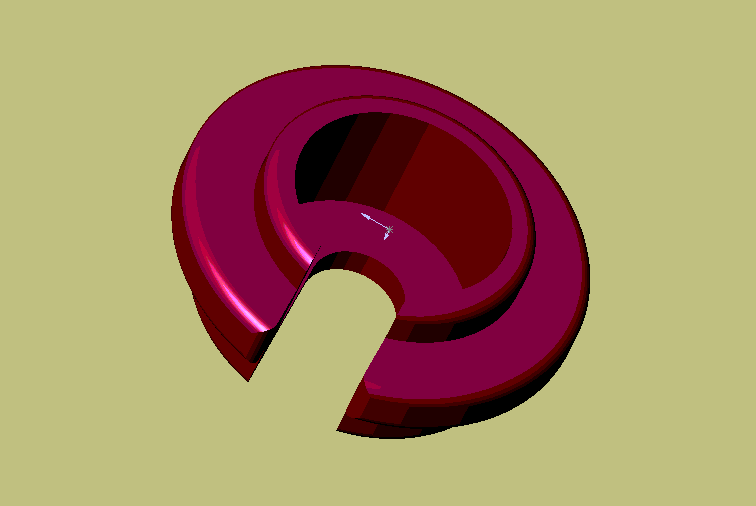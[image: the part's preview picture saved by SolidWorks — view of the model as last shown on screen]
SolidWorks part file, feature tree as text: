
SOLIDWORKS PART (.sldprt)
format: sldprt  version: not decoded by parser v0  size: 251,392 bytes
history: native  units: mm
features: sketch x5, plane x3, extrude x3, cut_extrude x2, material x1, fillet x1 (+8 scaffold rows collapsed)
feature tree (23):
  scaffold x8  (default folders/planes/origin — collapsed)
  material  "Matériau <non spécifié>"
  plane  "Plane1"
  plane  "Plane2"
  plane  "Plane3"
  sketch  "Esquisse1"  dims[D1=15.0mm]
  extrude  "Base-Extrusion"  Depth=2mm
  sketch  "Esquisse2"  dims[D1=12.0mm]
  extrude  "Boss.-Extru.1"  Depth=2.5mm
  sketch  "Esquisse3"  dims[D1=10.0mm]
  extrude  "Boss.-Extru.2"  Depth=1.5mm
  sketch  "Esquisse4"  dims[D1=8.0mm]
  cut_extrude  "Enlèv. mat.-Extru.1"  Depth=5mm
  sketch  "Esquisse5"  dims[D1=3.5mm]
  cut_extrude  "Enlèv. mat.-Extru.2"  [1 undecoded]
  fillet  "Congé3"  Radius=0.5mm
decode coverage: 10 of 11 modeling features carry decoded parameters
note: 1 parameter value undecoded
note: suppression state not decoded; provenance and decode notes live in map.json
